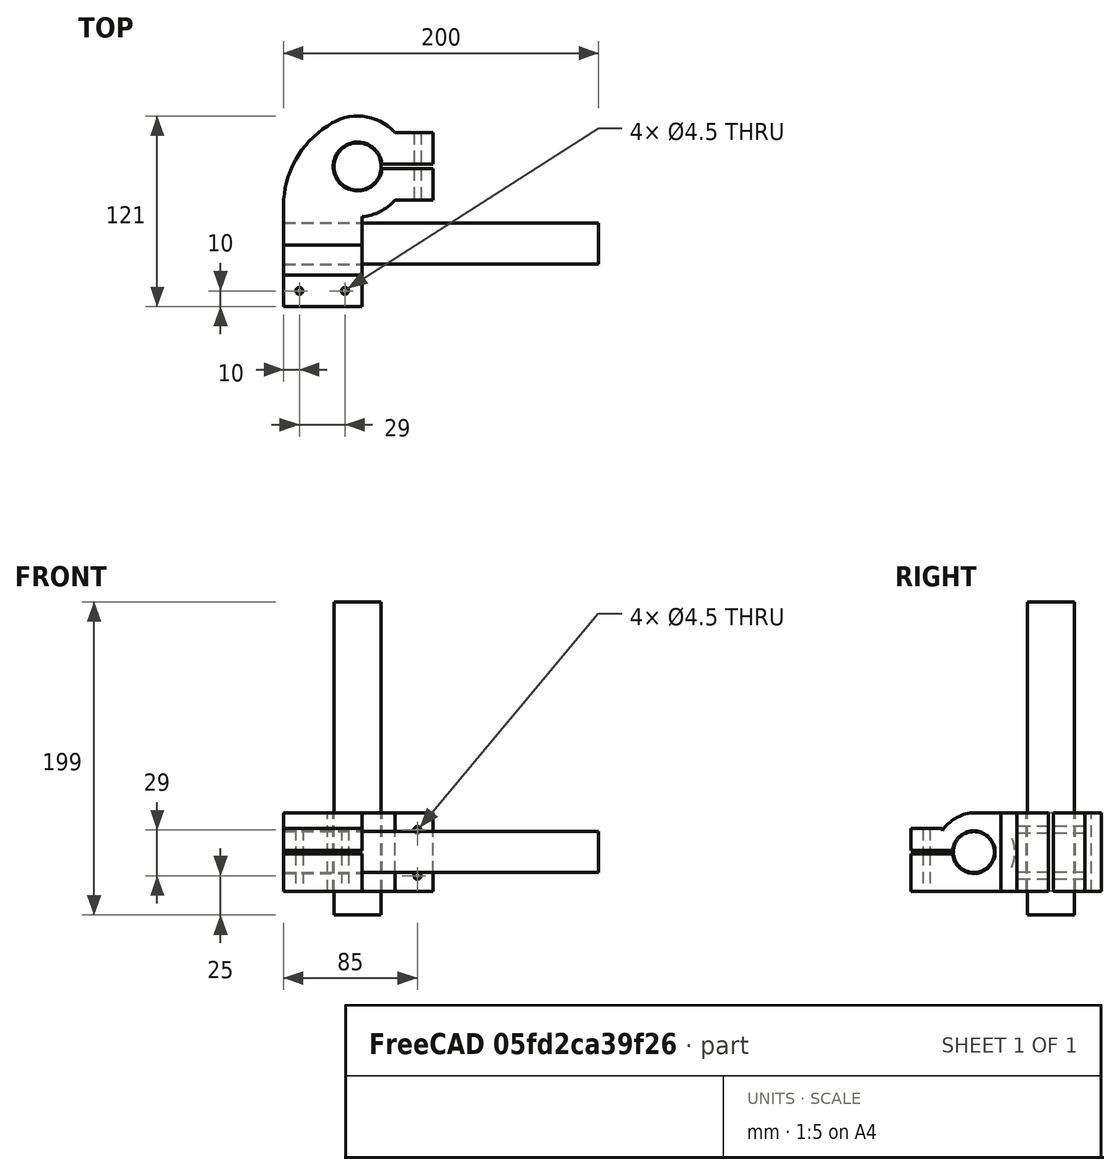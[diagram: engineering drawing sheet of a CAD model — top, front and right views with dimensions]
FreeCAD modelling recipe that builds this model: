
FCSTD DOCUMENT  (FreeCAD 0.19R24267 +99 (Git))
Label: CameraLeft
License: All rights reserved
LicenseURL: http://en.wikipedia.org/wiki/All_rights_reserved
objects: Part::Cylinder×9, Part::Box×8, Part::MultiFuse×4, Part::FeaturePython×2, Part::Cut×1
note: 24 computed .brp shape members not serialized (recipe doc carries the construction recipe); baked Part::Feature solids carry a one-line shape summary decoded from their .brp

FEATURE [Part::Cylinder] Cylinder  label="Horizontal"
  Angle = 360
  AttacherType = Attacher::AttachEngine3D
  Height = 199
  Radius = 15
FEATURE [Part::Cylinder] Cylinder001  label="Vertical"
  Angle = 360
  AttacherType = Attacher::AttachEngine3D
  Height = 200
  Placement = pos=(-47,-49,40) rot=(0.57735,0.57735,0.57735;2.0944rad)
  Radius = 13
FEATURE [Part::FeaturePython] Tube  label="TubeAddons"  # WARN: FeaturePython — macro-defined, semantics opaque (R4)
  AttacherType = Attacher::AttachEngine3D
  Height = 50
  InnerRadius = 15.5
  OuterRadius = 32
  Placement = pos=(0,0,15) rot=(0,0,1;0rad)
FEATURE [Part::FeaturePython] Tube001  label="TubeAddons001"  # WARN: FeaturePython — macro-defined, semantics opaque (R4)
  AttacherType = Attacher::AttachEngine3D
  Height = 50
  InnerRadius = 13.5
  OuterRadius = 25
  Placement = pos=(-47,-48,40) rot=(0,1,0;1.5708rad)
FEATURE [Part::Box] Box  label="horCuts"
  AttacherType = Attacher::AttachEngine3D
  Height = 50
  Length = 20
  Placement = pos=(14,-1.5,15) rot=(0,0,1;0rad)
  Width = 3
FEATURE [Part::Box] Box001  label="horAdd"
  AttacherType = Attacher::AttachEngine3D
  Height = 50
  Length = 25
  Placement = pos=(23,-21.5,15) rot=(0,0,1;0rad)
  Width = 20
FEATURE [Part::Box] Box002  label="horAdd001"
  AttacherType = Attacher::AttachEngine3D
  Height = 50
  Length = 25
  Placement = pos=(23,1.5,15) rot=(0,0,1;0rad)
  Width = 20
FEATURE [Part::Box] Box003  label="VerAddons"
  AttacherType = Attacher::AttachEngine3D
  Height = 10
  Length = 50
  Placement = pos=(-47,-89,15) rot=(0,0,1;0rad)
  Width = 63
FEATURE [Part::Box] Box004  label="VerAddons001"
  AttacherType = Attacher::AttachEngine3D
  Height = 14
  Length = 50
  Placement = pos=(-47,-89,25) rot=(0,0,1;0rad)
  Width = 25
FEATURE [Part::Box] Box005  label="VerAddons002"
  AttacherType = Attacher::AttachEngine3D
  Height = 14
  Length = 50
  Placement = pos=(-47,-89,41) rot=(0,0,1;0rad)
  Width = 20
FEATURE [Part::Box] Box006  label="verCuts"
  AttacherType = Attacher::AttachEngine3D
  Height = 2
  Length = 50
  Placement = pos=(-47,-89,39) rot=(0,0,1;0rad)
  Width = 27
FEATURE [Part::Cylinder] Cylinder002  label="AddCylinder"
  Angle = 60
  AttacherType = Attacher::AttachEngine3D
  Height = 50
  Placement = pos=(13,-25,15) rot=(0,0,1;2.0944rad)
  Radius = 60
FEATURE [Part::Box] Box007  label="VerAddons003"
  AttacherType = Attacher::AttachEngine3D
  Height = 50
  Length = 50
  Placement = pos=(-47,-50,15) rot=(0,0,1;0rad)
  Width = 25
FEATURE [Part::Cylinder] Cylinder003  label="Vertical001Cuts"
  Angle = 360
  AttacherType = Attacher::AttachEngine3D
  Height = 200
  Placement = pos=(-47,-49,40) rot=(0.57735,0.57735,0.57735;2.0944rad)
  Radius = 13.5
FEATURE [Part::Cylinder] Cylinder004  label="Horizontal001Cuts"
  Angle = 360
  AttacherType = Attacher::AttachEngine3D
  Height = 199
  Radius = 15.5
FEATURE [Part::Cylinder] Cylinder005  label="m4s"
  Angle = 360
  AttacherType = Attacher::AttachEngine3D
  Height = 50
  Placement = pos=(38,22,25) rot=(1,0,0;1.5708rad)
  Radius = 2.25
FEATURE [Part::Cylinder] Cylinder006  label="m4s001"
  Angle = 360
  AttacherType = Attacher::AttachEngine3D
  Height = 50
  Placement = pos=(38,22,54) rot=(1,0,0;1.5708rad)
  Radius = 2.25
FEATURE [Part::MultiFuse] Fusion  label="m4s002"
  Placement = pos=(-62,-117,43) rot=(0.57735,0.57735,0.57735;2.0944rad)
  Shapes = -> [Cylinder006,Cylinder005]
FEATURE [Part::Cylinder] Cylinder007  label="m4s004"
  Angle = 360
  AttacherType = Attacher::AttachEngine3D
  Height = 50
  Placement = pos=(38,22,25) rot=(1,0,0;1.5708rad)
  Radius = 2.25
FEATURE [Part::Cylinder] Cylinder008  label="m4s005"
  Angle = 360
  AttacherType = Attacher::AttachEngine3D
  Height = 50
  Placement = pos=(38,22,54) rot=(1,0,0;1.5708rad)
  Radius = 2.25
FEATURE [Part::MultiFuse] Fusion001  label="m4s003"
  Shapes = -> [Cylinder008,Cylinder007]
FEATURE [Part::MultiFuse] Fusion002  label="cuts"
  Shapes = -> [Box,Fusion,Fusion001,Cylinder004,Cylinder003,Box006]
FEATURE [Part::MultiFuse] Fusion003  label="Adds"
  Shapes = -> [Box007,Cylinder002,Box005,Box004,Box003,Box002,Box001,Tube001,Tube]
FEATURE [Part::Cut] Cut  label="left"
  Base = -> Fusion003
  Tool = -> Fusion002
